# Revit family: Zalustrowany_automatyczny_dozownik_mydla_i_srodkow_dezynfekcyjnych_1 l
name_source: partatom
category: Furniture
units: mm (PartAtom-declared; Revit-internal decimal feet)

## family parameters
Always vertical = Yes
Cut with Voids When Loaded = No
Host = Wall
Room Calculation Point = No
Shared = No

## types (1)
- SA1000BMJ
    Depth / Glebokosc = 120 mm  [stored 0.393701 ft]
    Description = Zalustrowy dozownik mydła w płynie to niezwykle trwały element nowoczesnej architektury łazienkowej. Podajniki zalustrowe cieszą się coraz większą popularnością we wnętrzach łazienek ogólnodostępnych. Montaż dozownika przeznaczonego do zabudowy za lustrem jest doskonałym rozwiązaniem do toalet w centrach handlowych, biurowcach, dworcach, hotelowym lobby.
    Height / Wysokosc = 320 mm  [stored 1.04987 ft]
    Manufacturer = FANECO.com
    Material = Stal nierdzewna AISI 304
    Material finish / Wykonczenie = Stal nierdzewna 304 szczotkowana, matowa
    Product code / Kod produktu = SA1000BMJ
    Type Comments = Zalustrowy automatyczny dozownik mydła w płynie i środków dezynfekcyjnych 1 l FANECO
    URL = https://faneco.com
    Weight / Waga = 7.2 kg
    Width / Szerokosc = 140 mm  [stored 0.459318 ft]

note: [stored X ft] marks values corroborated as IEEE doubles in the binary element streams (Revit-internal decimal feet)

## geometry (parser evidence)
native form markers: Sweep x6
no freeform markers — native parametric forms only
